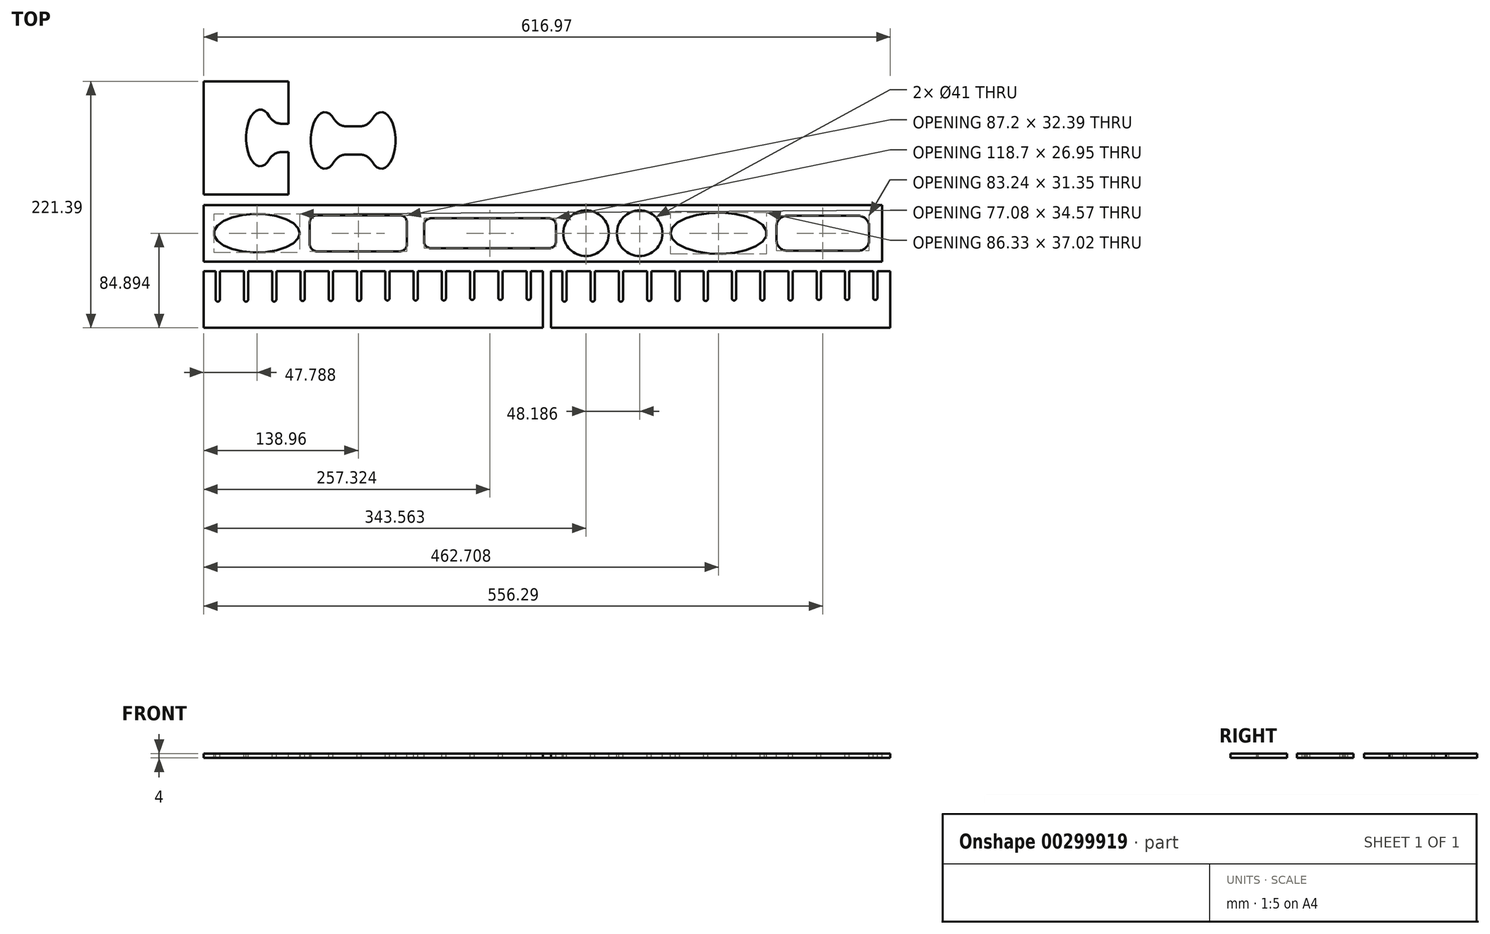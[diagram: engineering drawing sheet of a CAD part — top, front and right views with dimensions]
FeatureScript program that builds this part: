
annotation { "Feature Type Name" : "Feature", "Feature Type Description" : "" }
export const myFeature = defineFeature(function(context is Context, id is Id, definition is map)
    precondition{}
    {
        {
            var Q0;
            Q0=qCreatedBy(makeId("Top.planeOp"),FACE);
            var sketch = newSketch(context, id + "F0", { "sketchPlane" : qUnion([Q0])});
            skLineSegment(sketch, "E0.bottom", {"start": v(0, 119.79) * mm, "end": v(76.2, 119.79) * mm});
            skLineSegment(sketch, "E0.top", {"start": v(0, 221.39) * mm, "end": v(76.2, 221.39) * mm});
            skLineSegment(sketch, "E0.left", {"start": v(0, 119.79) * mm, "end": v(0, 221.39) * mm});
            skEllipticalArc(sketch, "E1", {});
            skLineSegment(sketch, "E2", {"start": v(0, 170.59) * mm, "end": v(76.2, 170.59) * mm, "construction": true});
            skLineSegment(sketch, "E3", {"start": v(70.2, 183.29) * mm, "end": v(76.2, 183.29) * mm});
            skLineSegment(sketch, "E4", {"start": v(70.2, 157.89) * mm, "end": v(76.2, 157.89) * mm});
            skLineSegment(sketch, "E5.trimOffspring", {"start": v(76.2, 183.29) * mm, "end": v(76.2, 221.39) * mm});
            skPoint(sketch, "E6.visualSharp", {"position": v(61.8, 183.29) * mm});
            skArc(sketch, "E6.filletArc", {"start": v(59.17, 189.7) * mm, "mid": v(63.82, 185) * mm, "end": v(70.2, 183.29) * mm});
            skPoint(sketch, "E7.visualSharp", {"position": v(61.8, 157.89) * mm});
            skArc(sketch, "E7.filletArc", {"start": v(70.2, 157.89) * mm, "mid": v(63.82, 156.17) * mm, "end": v(59.17, 151.48) * mm});
            skLineSegment(sketch, "E8", {"start": v(494.82, 175.08) * mm, "end": v(571.02, 175.08) * mm, "construction": true});
            skPoint(sketch, "E9.visualSharp", {"position": v(556.62, 187.78) * mm});
            skPoint(sketch, "E10.visualSharp", {"position": v(556.62, 162.38) * mm});
            skLineSegment(sketch, "E11", {"start": v(76.2, 157.89) * mm, "end": v(76.2, 119.79) * mm});
            skEllipticalArc(sketch, "E12", {});
            skLineSegment(sketch, "E13", {"start": v(128.28, 181) * mm, "end": v(134.28, 181) * mm});
            skLineSegment(sketch, "E14", {"start": v(128.28, 155.6) * mm, "end": v(134.28, 155.6) * mm});
            skPoint(sketch, "E15.visualSharp", {"position": v(119.88, 181) * mm});
            skArc(sketch, "E15.filletArc", {"start": v(117.25, 187.4) * mm, "mid": v(121.9, 182.71) * mm, "end": v(128.28, 181) * mm});
            skPoint(sketch, "E16.visualSharp", {"position": v(119.88, 155.6) * mm});
            skArc(sketch, "E16.filletArc", {"start": v(128.28, 155.6) * mm, "mid": v(121.9, 153.88) * mm, "end": v(117.25, 149.19) * mm});
            skLineSegment(sketch, "E17", {"start": v(134.28, 181) * mm, "end": v(134.28, 155.6) * mm, "construction": true});
            skLineSegment(sketch, "E18.MirrorCS", {"start": v(140.28, 155.6) * mm, "end": v(134.28, 155.6) * mm});
            skLineSegment(sketch, "E19.MirrorCS", {"start": v(140.28, 181) * mm, "end": v(134.28, 181) * mm});
            skArc(sketch, "E20.MirrorCS", {"start": v(151.3, 187.4) * mm, "mid": v(146.66, 182.71) * mm, "end": v(140.28, 181) * mm});
            skPoint(sketch, "E21.MirrorP", {"position": v(148.68, 181) * mm});
            skEllipticalArc(sketch, "E22.MirrorCS", {});
            skArc(sketch, "E23.MirrorCS", {"start": v(140.28, 155.6) * mm, "mid": v(146.66, 153.88) * mm, "end": v(151.3, 149.19) * mm});
            skPoint(sketch, "E24.MirrorP", {"position": v(148.68, 155.6) * mm});
            skLineSegment(sketch, "E25", {"start": v(190.41, 173.55) * mm, "end": v(266.61, 173.55) * mm, "construction": true});
            skPoint(sketch, "E26.visualSharp", {"position": v(252.21, 186.25) * mm});
            skPoint(sketch, "E27.visualSharp", {"position": v(252.21, 160.85) * mm});
            skLineSegment(sketch, "E28.0", {"start": v(190.44, 122.78) * mm, "end": v(190.44, 224.32) * mm});
            skLineSegment(sketch, "E28.1", {"start": v(190.44, 122.78) * mm, "end": v(266.59, 122.78) * mm});
            skLineSegment(sketch, "E28.2", {"start": v(190.44, 224.32) * mm, "end": v(266.59, 224.32) * mm});
            skLineSegment(sketch, "E28.3", {"start": v(266.59, 122.78) * mm, "end": v(266.59, 160.82) * mm});
            skLineSegment(sketch, "E28.4", {"start": v(260.61, 160.82) * mm, "end": v(266.59, 160.82) * mm});
            skArc(sketch, "E28.5", {"start": v(260.61, 160.82) * mm, "mid": v(254.25, 159.11) * mm, "end": v(249.6, 154.43) * mm});
            skLineSegment(sketch, "E28.6", {"start": v(266.59, 186.28) * mm, "end": v(266.59, 224.32) * mm});
            skLineSegment(sketch, "E28.7", {"start": v(260.61, 186.28) * mm, "end": v(266.59, 186.28) * mm});
            skArc(sketch, "E28.8", {"start": v(249.6, 192.67) * mm, "mid": v(254.25, 187.99) * mm, "end": v(260.61, 186.28) * mm});
            skFitSpline(sketch, "E28.9", {"points": [v(242.48, 198.9) * mm, v(241.21, 199.02) * mm, v(239.95, 198.9) * mm, v(238.3, 198.4) * mm, v(236.7, 197.43) * mm, v(235.2, 196.01) * mm, v(234.14, 194.73) * mm, v(233.3, 193.5) * mm, v(232.66, 192.4) * mm, v(232.2, 191.53) * mm, v(231.77, 190.61) * mm, v(231.23, 189.35) * mm, v(230.6, 187.67) * mm, v(229.97, 185.54) * mm, v(229.44, 183.3) * mm, v(229.02, 180.95) * mm, v(228.72, 178.54) * mm, v(228.56, 176.48) * mm, v(228.5, 174.81) * mm, v(228.48, 173.55) * mm, v(228.5, 172.29) * mm, v(228.56, 170.62) * mm, v(228.72, 168.56) * mm, v(229.02, 166.15) * mm, v(229.44, 163.8) * mm, v(229.97, 161.57) * mm, v(230.6, 159.43) * mm, v(231.23, 157.75) * mm, v(231.77, 156.49) * mm, v(232.2, 155.57) * mm, v(232.66, 154.7) * mm, v(233.3, 153.6) * mm, v(234.14, 152.37) * mm, v(235.2, 151.09) * mm, v(236.7, 149.67) * mm, v(238.3, 148.7) * mm, v(239.95, 148.2) * mm, v(241.21, 148.08) * mm, v(242.48, 148.2) * mm, v(244.13, 148.7) * mm, v(245.72, 149.67) * mm, v(247.22, 151.09) * mm, v(248.3, 152.37) * mm, v(249.13, 153.6) * mm, v(249.76, 154.7) * mm, v(250.22, 155.57) * mm, v(250.66, 156.49) * mm, v(251.2, 157.75) * mm, v(251.82, 159.43) * mm, v(252.46, 161.57) * mm, v(253, 163.8) * mm, v(253.4, 166.15) * mm, v(253.71, 168.56) * mm, v(253.87, 170.62) * mm, v(253.93, 172.29) * mm, v(253.94, 173.55) * mm, v(253.93, 174.81) * mm, v(253.87, 176.48) * mm, v(253.71, 178.54) * mm, v(253.4, 180.95) * mm, v(253, 183.3) * mm, v(252.46, 185.54) * mm, v(251.82, 187.67) * mm, v(251.2, 189.35) * mm, v(250.66, 190.61) * mm, v(250.22, 191.53) * mm, v(249.76, 192.4) * mm, v(249.13, 193.5) * mm, v(248.3, 194.73) * mm, v(247.22, 196.01) * mm, v(245.72, 197.43) * mm, v(244.13, 198.4) * mm, v(242.48, 198.9) * mm, v(241.21, 199.02) * mm, v(239.95, 198.9) * mm]});
            skFitSpline(sketch, "E29.9", {"points": [v(242.48, 198.9) * mm, v(241.21, 199.02) * mm, v(239.95, 198.9) * mm, v(238.3, 198.4) * mm, v(236.7, 197.43) * mm, v(235.2, 196.01) * mm, v(234.14, 194.73) * mm, v(233.3, 193.5) * mm, v(232.66, 192.4) * mm, v(232.2, 191.53) * mm, v(231.77, 190.61) * mm, v(231.23, 189.35) * mm, v(230.6, 187.67) * mm, v(229.97, 185.54) * mm, v(229.44, 183.3) * mm, v(229.02, 180.95) * mm, v(228.72, 178.54) * mm, v(228.56, 176.48) * mm, v(228.5, 174.81) * mm, v(228.48, 173.55) * mm, v(228.5, 172.29) * mm, v(228.56, 170.62) * mm, v(228.72, 168.56) * mm, v(229.02, 166.15) * mm, v(229.44, 163.8) * mm, v(229.97, 161.57) * mm, v(230.6, 159.43) * mm, v(231.23, 157.75) * mm, v(231.77, 156.49) * mm, v(232.2, 155.57) * mm, v(232.66, 154.7) * mm, v(233.3, 153.6) * mm, v(234.14, 152.37) * mm, v(235.2, 151.09) * mm, v(236.7, 149.67) * mm, v(238.3, 148.7) * mm, v(239.95, 148.2) * mm, v(241.21, 148.08) * mm, v(242.48, 148.2) * mm, v(244.13, 148.7) * mm, v(245.72, 149.67) * mm, v(247.22, 151.09) * mm, v(248.3, 152.37) * mm, v(249.13, 153.6) * mm, v(249.76, 154.7) * mm, v(250.22, 155.57) * mm, v(250.66, 156.49) * mm, v(251.2, 157.75) * mm, v(251.82, 159.43) * mm, v(252.46, 161.57) * mm, v(253, 163.8) * mm, v(253.4, 166.15) * mm, v(253.71, 168.56) * mm, v(253.87, 170.62) * mm, v(253.93, 172.29) * mm, v(253.94, 173.55) * mm, v(253.93, 174.81) * mm, v(253.87, 176.48) * mm, v(253.71, 178.54) * mm, v(253.4, 180.95) * mm, v(253, 183.3) * mm, v(252.46, 185.54) * mm, v(251.82, 187.67) * mm, v(251.2, 189.35) * mm, v(250.66, 190.61) * mm, v(250.22, 191.53) * mm, v(249.76, 192.4) * mm, v(249.13, 193.5) * mm, v(248.3, 194.73) * mm, v(247.22, 196.01) * mm, v(245.72, 197.43) * mm, v(244.13, 198.4) * mm, v(242.48, 198.9) * mm, v(241.21, 199.02) * mm, v(239.95, 198.9) * mm]});
            skLineSegment(sketch, "E30", {"start": v(291.99, 173.58) * mm, "end": v(368.19, 173.58) * mm, "construction": true});
            skPoint(sketch, "E31.visualSharp", {"position": v(353.79, 186.28) * mm});
            skPoint(sketch, "E32.visualSharp", {"position": v(353.79, 160.88) * mm});
            skLineSegment(sketch, "E33.0", {"start": v(292.04, 122.83) * mm, "end": v(292.04, 224.32) * mm});
            skLineSegment(sketch, "E33.1", {"start": v(292.04, 122.83) * mm, "end": v(368.14, 122.83) * mm});
            skLineSegment(sketch, "E33.2", {"start": v(292.04, 224.32) * mm, "end": v(368.14, 224.32) * mm});
            skLineSegment(sketch, "E33.3", {"start": v(368.14, 122.83) * mm, "end": v(368.14, 160.82) * mm});
            skLineSegment(sketch, "E33.4", {"start": v(362.19, 160.82) * mm, "end": v(368.14, 160.82) * mm});
            skArc(sketch, "E33.5", {"start": v(362.19, 160.82) * mm, "mid": v(355.84, 159.11) * mm, "end": v(351.2, 154.45) * mm});
            skLineSegment(sketch, "E33.6", {"start": v(368.14, 186.33) * mm, "end": v(368.14, 224.32) * mm});
            skLineSegment(sketch, "E33.7", {"start": v(362.19, 186.33) * mm, "end": v(368.14, 186.33) * mm});
            skArc(sketch, "E33.8", {"start": v(351.2, 192.7) * mm, "mid": v(355.84, 188.04) * mm, "end": v(362.19, 186.33) * mm});
            skFitSpline(sketch, "E33.9", {"points": [v(344.06, 198.94) * mm, v(342.79, 199.07) * mm, v(341.52, 198.94) * mm, v(339.86, 198.45) * mm, v(338.26, 197.47) * mm, v(336.76, 196.05) * mm, v(335.7, 194.77) * mm, v(334.85, 193.53) * mm, v(334.22, 192.44) * mm, v(333.76, 191.57) * mm, v(333.32, 190.65) * mm, v(332.78, 189.38) * mm, v(332.16, 187.7) * mm, v(331.52, 185.57) * mm, v(330.99, 183.32) * mm, v(330.57, 180.98) * mm, v(330.26, 178.57) * mm, v(330.11, 176.5) * mm, v(330.05, 174.84) * mm, v(330.03, 173.58) * mm, v(330.05, 172.31) * mm, v(330.11, 170.64) * mm, v(330.26, 168.58) * mm, v(330.57, 166.17) * mm, v(330.99, 163.83) * mm, v(331.52, 161.58) * mm, v(332.16, 159.45) * mm, v(332.78, 157.77) * mm, v(333.32, 156.5) * mm, v(333.76, 155.59) * mm, v(334.22, 154.71) * mm, v(334.85, 153.62) * mm, v(335.7, 152.38) * mm, v(336.76, 151.1) * mm, v(338.26, 149.68) * mm, v(339.86, 148.7) * mm, v(341.52, 148.2) * mm, v(342.79, 148.08) * mm, v(344.06, 148.2) * mm, v(345.72, 148.7) * mm, v(347.31, 149.68) * mm, v(348.82, 151.1) * mm, v(349.89, 152.38) * mm, v(350.73, 153.62) * mm, v(351.36, 154.71) * mm, v(351.82, 155.59) * mm, v(352.25, 156.5) * mm, v(352.8, 157.77) * mm, v(353.42, 159.45) * mm, v(354.06, 161.58) * mm, v(354.6, 163.83) * mm, v(355, 166.17) * mm, v(355.31, 168.58) * mm, v(355.47, 170.64) * mm, v(355.53, 172.31) * mm, v(355.54, 173.58) * mm, v(355.53, 174.84) * mm, v(355.47, 176.5) * mm, v(355.31, 178.57) * mm, v(355, 180.98) * mm, v(354.6, 183.32) * mm, v(354.06, 185.57) * mm, v(353.42, 187.7) * mm, v(352.8, 189.38) * mm, v(352.25, 190.65) * mm, v(351.82, 191.57) * mm, v(351.36, 192.44) * mm, v(350.73, 193.53) * mm, v(349.89, 194.77) * mm, v(348.82, 196.05) * mm, v(347.31, 197.47) * mm, v(345.72, 198.45) * mm, v(344.06, 198.94) * mm, v(342.79, 199.07) * mm, v(341.52, 198.94) * mm]});
            skLineSegment(sketch, "E34", {"start": v(400.26, 175.1) * mm, "end": v(476.46, 175.1) * mm, "construction": true});
            skPoint(sketch, "E35.visualSharp", {"position": v(462.06, 187.8) * mm});
            skPoint(sketch, "E36.visualSharp", {"position": v(462.06, 162.4) * mm});
            skLineSegment(sketch, "E37.0", {"start": v(400.33, 124.38) * mm, "end": v(400.33, 225.82) * mm});
            skLineSegment(sketch, "E37.1", {"start": v(400.33, 124.38) * mm, "end": v(476.38, 124.38) * mm});
            skLineSegment(sketch, "E37.2", {"start": v(400.33, 225.82) * mm, "end": v(476.38, 225.82) * mm});
            skLineSegment(sketch, "E37.3", {"start": v(476.38, 124.38) * mm, "end": v(476.38, 162.32) * mm});
            skLineSegment(sketch, "E37.4", {"start": v(470.46, 162.32) * mm, "end": v(476.38, 162.32) * mm});
            skArc(sketch, "E37.5", {"start": v(470.46, 162.32) * mm, "mid": v(464.12, 160.62) * mm, "end": v(459.5, 155.96) * mm});
            skLineSegment(sketch, "E37.6", {"start": v(476.38, 187.88) * mm, "end": v(476.38, 225.82) * mm});
            skLineSegment(sketch, "E37.7", {"start": v(470.46, 187.88) * mm, "end": v(476.38, 187.88) * mm});
            skArc(sketch, "E37.8", {"start": v(459.5, 194.24) * mm, "mid": v(464.12, 189.58) * mm, "end": v(470.46, 187.88) * mm});
            skFitSpline(sketch, "E37.9", {"points": [v(452.33, 200.5) * mm, v(451.06, 200.62) * mm, v(449.78, 200.5) * mm, v(448.12, 200) * mm, v(446.52, 199.02) * mm, v(445.01, 197.6) * mm, v(443.94, 196.31) * mm, v(443.1, 195.07) * mm, v(442.46, 193.98) * mm, v(442, 193.1) * mm, v(441.57, 192.19) * mm, v(441.02, 190.92) * mm, v(440.4, 189.24) * mm, v(439.76, 187.1) * mm, v(439.23, 184.85) * mm, v(438.81, 182.51) * mm, v(438.5, 180.1) * mm, v(438.35, 178.03) * mm, v(438.3, 176.36) * mm, v(438.28, 175.1) * mm, v(438.3, 173.84) * mm, v(438.35, 172.17) * mm, v(438.5, 170.1) * mm, v(438.81, 167.69) * mm, v(439.23, 165.35) * mm, v(439.76, 163.1) * mm, v(440.4, 160.96) * mm, v(441.02, 159.29) * mm, v(441.57, 158.02) * mm, v(442, 157.1) * mm, v(442.46, 156.23) * mm, v(443.1, 155.13) * mm, v(443.94, 153.89) * mm, v(445.01, 152.6) * mm, v(446.52, 151.18) * mm, v(448.12, 150.2) * mm, v(449.78, 149.7) * mm, v(451.06, 149.58) * mm, v(452.33, 149.7) * mm, v(454, 150.2) * mm, v(455.6, 151.18) * mm, v(457.1, 152.6) * mm, v(458.18, 153.89) * mm, v(459.02, 155.13) * mm, v(459.65, 156.23) * mm, v(460.1, 157.1) * mm, v(460.55, 158.02) * mm, v(461.1, 159.29) * mm, v(461.71, 160.96) * mm, v(462.35, 163.1) * mm, v(462.88, 165.35) * mm, v(463.3, 167.69) * mm, v(463.6, 170.1) * mm, v(463.76, 172.17) * mm, v(463.82, 173.84) * mm, v(463.84, 175.1) * mm, v(463.82, 176.36) * mm, v(463.76, 178.03) * mm, v(463.6, 180.1) * mm, v(463.3, 182.51) * mm, v(462.88, 184.85) * mm, v(462.35, 187.1) * mm, v(461.71, 189.24) * mm, v(461.1, 190.92) * mm, v(460.55, 192.19) * mm, v(460.1, 193.1) * mm, v(459.65, 193.98) * mm, v(459.02, 195.07) * mm, v(458.18, 196.31) * mm, v(457.1, 197.6) * mm, v(455.6, 199.02) * mm, v(454, 200) * mm, v(452.33, 200.5) * mm, v(451.06, 200.62) * mm, v(449.78, 200.5) * mm]});
            skLineSegment(sketch, "E38.0", {"start": v(494.92, 124.38) * mm, "end": v(494.92, 225.77) * mm});
            skLineSegment(sketch, "E38.1", {"start": v(494.92, 124.38) * mm, "end": v(570.92, 124.38) * mm});
            skLineSegment(sketch, "E38.2", {"start": v(494.92, 225.77) * mm, "end": v(570.92, 225.77) * mm});
            skLineSegment(sketch, "E38.3", {"start": v(570.92, 124.38) * mm, "end": v(570.92, 162.27) * mm});
            skLineSegment(sketch, "E38.4", {"start": v(565.02, 162.27) * mm, "end": v(570.92, 162.27) * mm});
            skArc(sketch, "E38.5", {"start": v(565.02, 162.27) * mm, "mid": v(558.7, 160.57) * mm, "end": v(554.08, 155.92) * mm});
            skLineSegment(sketch, "E38.6", {"start": v(570.92, 187.88) * mm, "end": v(570.92, 225.77) * mm});
            skLineSegment(sketch, "E38.7", {"start": v(565.02, 187.88) * mm, "end": v(570.92, 187.88) * mm});
            skArc(sketch, "E38.8", {"start": v(554.08, 194.23) * mm, "mid": v(558.7, 189.58) * mm, "end": v(565.02, 187.88) * mm});
            skFitSpline(sketch, "E38.9", {"points": [v(546.9, 200.5) * mm, v(545.62, 200.62) * mm, v(544.34, 200.5) * mm, v(542.67, 200) * mm, v(541.07, 199.01) * mm, v(539.56, 197.59) * mm, v(538.48, 196.3) * mm, v(537.64, 195.06) * mm, v(537, 193.96) * mm, v(536.55, 193.09) * mm, v(536.11, 192.17) * mm, v(535.56, 190.9) * mm, v(534.94, 189.22) * mm, v(534.3, 187.08) * mm, v(533.77, 184.83) * mm, v(533.35, 182.5) * mm, v(533.05, 180.07) * mm, v(532.9, 178.01) * mm, v(532.83, 176.34) * mm, v(532.82, 175.08) * mm, v(532.83, 173.81) * mm, v(532.9, 172.14) * mm, v(533.05, 170.08) * mm, v(533.35, 167.66) * mm, v(533.77, 165.32) * mm, v(534.3, 163.07) * mm, v(534.94, 160.93) * mm, v(535.56, 159.25) * mm, v(536.11, 157.98) * mm, v(536.55, 157.06) * mm, v(537, 156.19) * mm, v(537.64, 155.1) * mm, v(538.48, 153.85) * mm, v(539.56, 152.56) * mm, v(541.07, 151.14) * mm, v(542.67, 150.16) * mm, v(544.34, 149.66) * mm, v(545.62, 149.53) * mm, v(546.9, 149.66) * mm, v(548.57, 150.16) * mm, v(550.18, 151.14) * mm, v(551.69, 152.56) * mm, v(552.76, 153.85) * mm, v(553.6, 155.1) * mm, v(554.24, 156.19) * mm, v(554.7, 157.06) * mm, v(555.13, 157.98) * mm, v(555.68, 159.25) * mm, v(556.3, 160.93) * mm, v(556.94, 163.07) * mm, v(557.47, 165.32) * mm, v(557.9, 167.66) * mm, v(558.2, 170.08) * mm, v(558.35, 172.14) * mm, v(558.41, 173.81) * mm, v(558.43, 175.08) * mm, v(558.41, 176.34) * mm, v(558.35, 178.01) * mm, v(558.2, 180.07) * mm, v(557.9, 182.5) * mm, v(557.47, 184.83) * mm, v(556.94, 187.08) * mm, v(556.3, 189.22) * mm, v(555.68, 190.9) * mm, v(555.13, 192.17) * mm, v(554.7, 193.09) * mm, v(554.24, 193.96) * mm, v(553.6, 195.06) * mm, v(552.76, 196.3) * mm, v(551.69, 197.59) * mm, v(550.18, 199.01) * mm, v(548.57, 200) * mm, v(546.9, 200.5) * mm, v(545.62, 200.62) * mm, v(544.34, 200.5) * mm]});
            skLineSegment(sketch, "E39.bottom", {"start": v(0, 0) * mm, "end": v(304.8, 0) * mm});
            skLineSegment(sketch, "E39.top", {"start": v(0, 50.8) * mm, "end": v(10.75, 50.8) * mm});
            skLineSegment(sketch, "E39.left", {"start": v(0, 0) * mm, "end": v(0, 50.8) * mm});
            skLineSegment(sketch, "E39.right", {"start": v(304.8, 0) * mm, "end": v(304.8, 50.8) * mm});
            skLineSegment(sketch, "E40.direction1", {"start": v(12.64, 25.4) * mm, "end": v(38.04, 25.4) * mm, "construction": true});
            skArc(sketch, "E41.0.endCap", {"start": v(14.54, 25.4) * mm, "mid": v(12.64, 23.5) * mm, "end": v(10.75, 25.4) * mm});
            skLineSegment(sketch, "E41.0.left", {"start": v(14.54, 50.8) * mm, "end": v(14.54, 25.4) * mm});
            skLineSegment(sketch, "E41.0.right", {"start": v(10.75, 50.8) * mm, "end": v(10.75, 25.4) * mm});
            skArc(sketch, "E42.0.endCap", {"start": v(39.94, 25.4) * mm, "mid": v(38.04, 23.5) * mm, "end": v(36.14, 25.4) * mm});
            skLineSegment(sketch, "E42.0.left", {"start": v(39.94, 50.8) * mm, "end": v(39.94, 25.4) * mm});
            skLineSegment(sketch, "E42.0.right", {"start": v(36.14, 50.8) * mm, "end": v(36.14, 25.4) * mm});
            skArc(sketch, "E43.0.endCap", {"start": v(65.26, 25.4) * mm, "mid": v(63.35, 23.5) * mm, "end": v(61.45, 25.4) * mm});
            skLineSegment(sketch, "E43.0.left", {"start": v(65.26, 50.8) * mm, "end": v(65.26, 25.4) * mm});
            skLineSegment(sketch, "E43.0.right", {"start": v(61.45, 50.8) * mm, "end": v(61.45, 25.4) * mm});
            skLineSegment(sketch, "E44.direction1", {"start": v(88.85, 25.9) * mm, "end": v(114.25, 25.9) * mm, "construction": true});
            skArc(sketch, "E45.0.endCap", {"start": v(90.74, 25.9) * mm, "mid": v(88.85, 24) * mm, "end": v(86.95, 25.9) * mm});
            skLineSegment(sketch, "E45.0.left", {"start": v(90.74, 50.8) * mm, "end": v(90.74, 25.9) * mm});
            skLineSegment(sketch, "E45.0.right", {"start": v(86.95, 50.8) * mm, "end": v(86.95, 25.9) * mm});
            skArc(sketch, "E46.0.endCap", {"start": v(116.15, 25.9) * mm, "mid": v(114.25, 24) * mm, "end": v(112.35, 25.9) * mm});
            skLineSegment(sketch, "E46.0.left", {"start": v(116.15, 50.8) * mm, "end": v(116.15, 25.9) * mm});
            skLineSegment(sketch, "E46.0.right", {"start": v(112.35, 50.8) * mm, "end": v(112.35, 25.9) * mm});
            skArc(sketch, "E47.0.endCap", {"start": v(141.46, 25.9) * mm, "mid": v(139.56, 24) * mm, "end": v(137.65, 25.9) * mm});
            skLineSegment(sketch, "E47.0.left", {"start": v(141.46, 50.8) * mm, "end": v(141.46, 25.9) * mm});
            skLineSegment(sketch, "E47.0.right", {"start": v(137.65, 50.8) * mm, "end": v(137.65, 25.9) * mm});
            skLineSegment(sketch, "E48.direction1", {"start": v(165.05, 26.4) * mm, "end": v(190.45, 26.4) * mm, "construction": true});
            skArc(sketch, "E49.0.endCap", {"start": v(166.94, 26.4) * mm, "mid": v(165.05, 24.5) * mm, "end": v(163.15, 26.4) * mm});
            skLineSegment(sketch, "E49.0.left", {"start": v(166.94, 50.8) * mm, "end": v(166.94, 26.4) * mm});
            skLineSegment(sketch, "E49.0.right", {"start": v(163.15, 50.8) * mm, "end": v(163.15, 26.4) * mm});
            skArc(sketch, "E50.0.endCap", {"start": v(192.35, 26.4) * mm, "mid": v(190.45, 24.5) * mm, "end": v(188.55, 26.4) * mm});
            skLineSegment(sketch, "E50.0.left", {"start": v(192.35, 50.8) * mm, "end": v(192.35, 26.4) * mm});
            skLineSegment(sketch, "E50.0.right", {"start": v(188.55, 50.8) * mm, "end": v(188.55, 26.4) * mm});
            skArc(sketch, "E51.0.endCap", {"start": v(217.66, 26.4) * mm, "mid": v(215.75, 24.5) * mm, "end": v(213.85, 26.4) * mm});
            skLineSegment(sketch, "E51.0.left", {"start": v(217.66, 50.8) * mm, "end": v(217.66, 26.4) * mm});
            skLineSegment(sketch, "E51.0.right", {"start": v(213.85, 50.8) * mm, "end": v(213.85, 26.4) * mm});
            skLineSegment(sketch, "E52.direction1", {"start": v(241.25, 26.9) * mm, "end": v(266.64, 26.9) * mm, "construction": true});
            skArc(sketch, "E53.0.endCap", {"start": v(243.14, 26.9) * mm, "mid": v(241.25, 25) * mm, "end": v(239.35, 26.9) * mm});
            skLineSegment(sketch, "E53.0.left", {"start": v(243.14, 50.8) * mm, "end": v(243.14, 26.9) * mm});
            skLineSegment(sketch, "E53.0.right", {"start": v(239.35, 50.8) * mm, "end": v(239.35, 26.9) * mm});
            skArc(sketch, "E54.0.endCap", {"start": v(268.54, 26.9) * mm, "mid": v(266.64, 25) * mm, "end": v(264.75, 26.9) * mm});
            skLineSegment(sketch, "E54.0.left", {"start": v(268.54, 50.8) * mm, "end": v(268.54, 26.9) * mm});
            skLineSegment(sketch, "E54.0.right", {"start": v(264.74, 50.8) * mm, "end": v(264.74, 26.9) * mm});
            skArc(sketch, "E55.0.endCap", {"start": v(293.86, 26.9) * mm, "mid": v(291.96, 25) * mm, "end": v(290.05, 26.9) * mm});
            skLineSegment(sketch, "E55.0.left", {"start": v(293.86, 50.8) * mm, "end": v(293.86, 26.9) * mm});
            skLineSegment(sketch, "E55.0.right", {"start": v(290.05, 50.8) * mm, "end": v(290.05, 26.9) * mm});
            skLineSegment(sketch, "E56.trimOffspring", {"start": v(14.54, 50.8) * mm, "end": v(36.14, 50.8) * mm});
            skLineSegment(sketch, "E57.trimOffspring", {"start": v(39.94, 50.8) * mm, "end": v(61.45, 50.8) * mm});
            skLineSegment(sketch, "E58.trimOffspring", {"start": v(65.26, 50.8) * mm, "end": v(86.95, 50.8) * mm});
            skLineSegment(sketch, "E59.trimOffspring", {"start": v(90.74, 50.8) * mm, "end": v(112.35, 50.8) * mm});
            skLineSegment(sketch, "E60.trimOffspring", {"start": v(116.15, 50.8) * mm, "end": v(137.65, 50.8) * mm});
            skLineSegment(sketch, "E61.trimOffspring", {"start": v(141.46, 50.8) * mm, "end": v(163.15, 50.8) * mm});
            skLineSegment(sketch, "E62.trimOffspring", {"start": v(166.94, 50.8) * mm, "end": v(188.55, 50.8) * mm});
            skLineSegment(sketch, "E63.trimOffspring", {"start": v(192.35, 50.8) * mm, "end": v(213.85, 50.8) * mm});
            skLineSegment(sketch, "E64.trimOffspring", {"start": v(217.66, 50.8) * mm, "end": v(239.35, 50.8) * mm});
            skLineSegment(sketch, "E65.trimOffspring", {"start": v(243.14, 50.8) * mm, "end": v(264.74, 50.8) * mm});
            skLineSegment(sketch, "E66.trimOffspring", {"start": v(268.54, 50.8) * mm, "end": v(290.05, 50.8) * mm});
            skLineSegment(sketch, "E67.trimOffspring", {"start": v(293.86, 50.8) * mm, "end": v(304.8, 50.8) * mm});
            skLineSegment(sketch, "E68.bottom", {"start": v(0, 59.5) * mm, "end": v(609.6, 59.5) * mm});
            skLineSegment(sketch, "E68.top", {"start": v(0, 110.3) * mm, "end": v(609.6, 110.3) * mm});
            skLineSegment(sketch, "E68.left", {"start": v(0, 59.5) * mm, "end": v(0, 110.3) * mm});
            skLineSegment(sketch, "E68.right", {"start": v(609.6, 59.5) * mm, "end": v(609.6, 110.3) * mm});
            skEllipse(sketch, "E69", {"center": v(47.79, 84.9) * mm, "majorRadius": 38.54 * mm, "minorRadius": 17.29 * mm, "majorAxis": v(1, 0)});
            skPoint(sketch, "E69.centerSnap0", {"position": v(0, 84.9) * mm});
            skLineSegment(sketch, "E70.bottom", {"start": v(101.7, 101.09) * mm, "end": v(176.21, 101.09) * mm});
            skLineSegment(sketch, "E70.top", {"start": v(101.7, 68.7) * mm, "end": v(176.21, 68.7) * mm});
            skLineSegment(sketch, "E70.left", {"start": v(95.36, 94.74) * mm, "end": v(95.36, 75.05) * mm});
            skLineSegment(sketch, "E70.right", {"start": v(182.56, 94.74) * mm, "end": v(182.56, 75.05) * mm});
            skPoint(sketch, "E70.middle", {"position": v(138.96, 84.9) * mm});
            skPoint(sketch, "E70.middle.positionSnap0", {"position": v(86.33, 84.9) * mm});
            skPoint(sketch, "E70.centerSnap0", {"position": v(86.33, 84.9) * mm});
            skPoint(sketch, "E71.visualSharp", {"position": v(95.36, 101.09) * mm});
            skArc(sketch, "E71.filletArc", {"start": v(101.7, 101.09) * mm, "mid": v(97.22, 99.23) * mm, "end": v(95.36, 94.74) * mm});
            skPoint(sketch, "E72.visualSharp", {"position": v(182.56, 101.09) * mm});
            skArc(sketch, "E72.filletArc", {"start": v(182.56, 94.74) * mm, "mid": v(180.7, 99.23) * mm, "end": v(176.21, 101.09) * mm});
            skPoint(sketch, "E73.visualSharp", {"position": v(182.56, 68.7) * mm});
            skArc(sketch, "E73.filletArc", {"start": v(176.21, 68.7) * mm, "mid": v(180.7, 70.56) * mm, "end": v(182.56, 75.05) * mm});
            skPoint(sketch, "E74.visualSharp", {"position": v(95.36, 68.7) * mm});
            skArc(sketch, "E74.filletArc", {"start": v(95.36, 75.05) * mm, "mid": v(97.22, 70.56) * mm, "end": v(101.7, 68.7) * mm});
            skLineSegment(sketch, "E75.bottom", {"start": v(204.32, 98.37) * mm, "end": v(310.32, 98.37) * mm});
            skLineSegment(sketch, "E75.top", {"start": v(204.32, 71.42) * mm, "end": v(310.32, 71.42) * mm});
            skLineSegment(sketch, "E75.left", {"start": v(197.97, 92.02) * mm, "end": v(197.97, 77.77) * mm});
            skLineSegment(sketch, "E75.right", {"start": v(316.67, 92.02) * mm, "end": v(316.67, 77.77) * mm});
            skPoint(sketch, "E75.middle", {"position": v(257.32, 84.9) * mm});
            skPoint(sketch, "E75.middle.positionSnap0", {"position": v(182.56, 84.9) * mm});
            skPoint(sketch, "E75.centerSnap0", {"position": v(182.56, 84.9) * mm});
            skPoint(sketch, "E76.visualSharp", {"position": v(197.97, 98.37) * mm});
            skArc(sketch, "E76.filletArc", {"start": v(204.32, 98.37) * mm, "mid": v(199.83, 96.51) * mm, "end": v(197.97, 92.02) * mm});
            skPoint(sketch, "E77.visualSharp", {"position": v(197.97, 71.42) * mm});
            skArc(sketch, "E77.filletArc", {"start": v(197.97, 77.77) * mm, "mid": v(199.83, 73.28) * mm, "end": v(204.32, 71.42) * mm});
            skPoint(sketch, "E78.visualSharp", {"position": v(316.67, 71.42) * mm});
            skArc(sketch, "E78.filletArc", {"start": v(310.32, 71.42) * mm, "mid": v(314.81, 73.28) * mm, "end": v(316.67, 77.77) * mm});
            skPoint(sketch, "E79.visualSharp", {"position": v(316.67, 98.37) * mm});
            skArc(sketch, "E79.filletArc", {"start": v(316.67, 92.02) * mm, "mid": v(314.81, 96.51) * mm, "end": v(310.32, 98.37) * mm});
            skCircle(sketch, "E80", {"center": v(343.56, 84.9) * mm, "radius": 20.5 * mm});
            skCircle(sketch, "E81", {"center": v(391.75, 84.9) * mm, "radius": 20.5 * mm});
            skEllipse(sketch, "E82", {"center": v(462.7, 84.9) * mm, "majorRadius": 43.16 * mm, "minorRadius": 18.51 * mm, "majorAxis": v(-1, 0)});
            skPoint(sketch, "E82.centerSnap0", {"position": v(609.6, 84.9) * mm});
            skLineSegment(sketch, "E83.bottom", {"start": v(524.2, 100.57) * mm, "end": v(588.39, 100.57) * mm});
            skLineSegment(sketch, "E83.top", {"start": v(524.2, 69.22) * mm, "end": v(588.39, 69.22) * mm});
            skLineSegment(sketch, "E83.left", {"start": v(514.67, 91.04) * mm, "end": v(514.67, 78.75) * mm});
            skLineSegment(sketch, "E83.right", {"start": v(597.91, 91.04) * mm, "end": v(597.91, 78.75) * mm});
            skPoint(sketch, "E83.middle", {"position": v(556.3, 84.9) * mm});
            skPoint(sketch, "E84.visualSharp", {"position": v(514.67, 100.57) * mm});
            skArc(sketch, "E84.filletArc", {"start": v(524.2, 100.57) * mm, "mid": v(517.46, 97.78) * mm, "end": v(514.67, 91.04) * mm});
            skPoint(sketch, "E85.visualSharp", {"position": v(597.91, 100.57) * mm});
            skArc(sketch, "E85.filletArc", {"start": v(597.91, 91.04) * mm, "mid": v(595.12, 97.78) * mm, "end": v(588.39, 100.57) * mm});
            skPoint(sketch, "E86.visualSharp", {"position": v(597.91, 69.22) * mm});
            skArc(sketch, "E86.filletArc", {"start": v(588.39, 69.22) * mm, "mid": v(595.12, 72.01) * mm, "end": v(597.91, 78.75) * mm});
            skPoint(sketch, "E87.visualSharp", {"position": v(514.67, 69.22) * mm});
            skArc(sketch, "E87.filletArc", {"start": v(514.67, 78.75) * mm, "mid": v(517.46, 72.01) * mm, "end": v(524.2, 69.22) * mm});
            skLineSegment(sketch, "E88.bottom", {"start": v(312.17, 0) * mm, "end": v(616.97, 0) * mm});
            skLineSegment(sketch, "E88.top", {"start": v(312.17, 50.8) * mm, "end": v(322.27, 50.8) * mm});
            skLineSegment(sketch, "E88.left", {"start": v(312.17, 0) * mm, "end": v(312.17, 50.8) * mm});
            skLineSegment(sketch, "E88.right", {"start": v(616.97, 0) * mm, "end": v(616.97, 50.8) * mm});
            skLineSegment(sketch, "E89.direction1", {"start": v(324.16, 25.4) * mm, "end": v(349.56, 25.4) * mm, "construction": true});
            skArc(sketch, "E90.0.endCap", {"start": v(326.06, 25.4) * mm, "mid": v(324.16, 23.5) * mm, "end": v(322.27, 25.4) * mm});
            skLineSegment(sketch, "E90.0.left", {"start": v(326.06, 50.8) * mm, "end": v(326.06, 25.4) * mm});
            skLineSegment(sketch, "E90.0.right", {"start": v(322.27, 50.8) * mm, "end": v(322.27, 25.4) * mm});
            skArc(sketch, "E91.0.endCap", {"start": v(351.46, 25.4) * mm, "mid": v(349.56, 23.5) * mm, "end": v(347.66, 25.4) * mm});
            skLineSegment(sketch, "E91.0.left", {"start": v(351.46, 50.8) * mm, "end": v(351.46, 25.4) * mm});
            skLineSegment(sketch, "E91.0.right", {"start": v(347.66, 50.8) * mm, "end": v(347.66, 25.4) * mm});
            skArc(sketch, "E92.0.endCap", {"start": v(376.78, 25.4) * mm, "mid": v(374.87, 23.5) * mm, "end": v(372.97, 25.4) * mm});
            skLineSegment(sketch, "E92.0.left", {"start": v(376.78, 50.8) * mm, "end": v(376.78, 25.4) * mm});
            skLineSegment(sketch, "E92.0.right", {"start": v(372.97, 50.8) * mm, "end": v(372.97, 25.4) * mm});
            skLineSegment(sketch, "E93.direction1", {"start": v(400.36, 25.9) * mm, "end": v(425.76, 25.9) * mm, "construction": true});
            skArc(sketch, "E94.0.endCap", {"start": v(402.26, 25.9) * mm, "mid": v(400.36, 24) * mm, "end": v(398.47, 25.9) * mm});
            skLineSegment(sketch, "E94.0.left", {"start": v(402.26, 50.8) * mm, "end": v(402.26, 25.9) * mm});
            skLineSegment(sketch, "E94.0.right", {"start": v(398.47, 50.8) * mm, "end": v(398.47, 25.9) * mm});
            skArc(sketch, "E95.0.endCap", {"start": v(427.66, 25.9) * mm, "mid": v(425.76, 24) * mm, "end": v(423.86, 25.9) * mm});
            skLineSegment(sketch, "E95.0.left", {"start": v(427.66, 50.8) * mm, "end": v(427.66, 25.9) * mm});
            skLineSegment(sketch, "E95.0.right", {"start": v(423.86, 50.8) * mm, "end": v(423.86, 25.9) * mm});
            skArc(sketch, "E96.0.endCap", {"start": v(452.98, 25.9) * mm, "mid": v(451.07, 24) * mm, "end": v(449.17, 25.9) * mm});
            skLineSegment(sketch, "E96.0.left", {"start": v(452.98, 50.8) * mm, "end": v(452.98, 25.9) * mm});
            skLineSegment(sketch, "E96.0.right", {"start": v(449.17, 50.8) * mm, "end": v(449.17, 25.9) * mm});
            skLineSegment(sketch, "E97.direction1", {"start": v(476.56, 26.4) * mm, "end": v(501.96, 26.4) * mm, "construction": true});
            skArc(sketch, "E98.0.endCap", {"start": v(478.46, 26.4) * mm, "mid": v(476.56, 24.5) * mm, "end": v(474.67, 26.4) * mm});
            skLineSegment(sketch, "E98.0.left", {"start": v(478.46, 50.8) * mm, "end": v(478.46, 26.4) * mm});
            skLineSegment(sketch, "E98.0.right", {"start": v(474.67, 50.8) * mm, "end": v(474.67, 26.4) * mm});
            skArc(sketch, "E99.0.endCap", {"start": v(503.86, 26.4) * mm, "mid": v(501.96, 24.5) * mm, "end": v(500.06, 26.4) * mm});
            skLineSegment(sketch, "E99.0.left", {"start": v(503.86, 50.8) * mm, "end": v(503.86, 26.4) * mm});
            skLineSegment(sketch, "E99.0.right", {"start": v(500.06, 50.8) * mm, "end": v(500.06, 26.4) * mm});
            skArc(sketch, "E100.0.endCap", {"start": v(529.18, 26.4) * mm, "mid": v(527.27, 24.5) * mm, "end": v(525.37, 26.4) * mm});
            skLineSegment(sketch, "E100.0.left", {"start": v(529.18, 50.8) * mm, "end": v(529.18, 26.4) * mm});
            skLineSegment(sketch, "E100.0.right", {"start": v(525.37, 50.8) * mm, "end": v(525.37, 26.4) * mm});
            skLineSegment(sketch, "E101.direction1", {"start": v(552.76, 26.9) * mm, "end": v(578.16, 26.9) * mm, "construction": true});
            skArc(sketch, "E102.0.endCap", {"start": v(554.66, 26.9) * mm, "mid": v(552.76, 25) * mm, "end": v(550.87, 26.9) * mm});
            skLineSegment(sketch, "E102.0.left", {"start": v(554.66, 50.8) * mm, "end": v(554.66, 26.9) * mm});
            skLineSegment(sketch, "E102.0.right", {"start": v(550.87, 50.8) * mm, "end": v(550.87, 26.9) * mm});
            skArc(sketch, "E103.0.endCap", {"start": v(580.06, 26.9) * mm, "mid": v(578.16, 25) * mm, "end": v(576.26, 26.9) * mm});
            skLineSegment(sketch, "E103.0.left", {"start": v(580.06, 50.8) * mm, "end": v(580.06, 26.9) * mm});
            skLineSegment(sketch, "E103.0.right", {"start": v(576.26, 50.8) * mm, "end": v(576.26, 26.9) * mm});
            skArc(sketch, "E104.0.endCap", {"start": v(605.38, 26.9) * mm, "mid": v(603.47, 25) * mm, "end": v(601.57, 26.9) * mm});
            skLineSegment(sketch, "E104.0.left", {"start": v(605.38, 50.8) * mm, "end": v(605.38, 26.9) * mm});
            skLineSegment(sketch, "E104.0.right", {"start": v(601.57, 50.8) * mm, "end": v(601.57, 26.9) * mm});
            skLineSegment(sketch, "E105.trimOffspring", {"start": v(326.06, 50.8) * mm, "end": v(347.66, 50.8) * mm});
            skLineSegment(sketch, "E106.trimOffspring", {"start": v(351.46, 50.8) * mm, "end": v(372.97, 50.8) * mm});
            skLineSegment(sketch, "E107.trimOffspring", {"start": v(376.78, 50.8) * mm, "end": v(398.47, 50.8) * mm});
            skLineSegment(sketch, "E108.trimOffspring", {"start": v(402.26, 50.8) * mm, "end": v(423.86, 50.8) * mm});
            skLineSegment(sketch, "E109.trimOffspring", {"start": v(427.66, 50.8) * mm, "end": v(449.17, 50.8) * mm});
            skLineSegment(sketch, "E110.trimOffspring", {"start": v(452.98, 50.8) * mm, "end": v(474.67, 50.8) * mm});
            skLineSegment(sketch, "E111.trimOffspring", {"start": v(478.46, 50.8) * mm, "end": v(500.06, 50.8) * mm});
            skLineSegment(sketch, "E112.trimOffspring", {"start": v(503.86, 50.8) * mm, "end": v(525.37, 50.8) * mm});
            skLineSegment(sketch, "E113.trimOffspring", {"start": v(529.18, 50.8) * mm, "end": v(550.87, 50.8) * mm});
            skLineSegment(sketch, "E114.trimOffspring", {"start": v(554.66, 50.8) * mm, "end": v(576.26, 50.8) * mm});
            skLineSegment(sketch, "E115.trimOffspring", {"start": v(580.06, 50.8) * mm, "end": v(601.57, 50.8) * mm});
            skLineSegment(sketch, "E116.trimOffspring", {"start": v(605.38, 50.8) * mm, "end": v(616.97, 50.8) * mm});
            const initialGuessF0  = {"E1": [0.0508, 0.17058822201490403, 0, 1, 0.0254, 0.0127, 5.563731595720363, 3.8610463650490146], "E12": [0.10887801727700261, 0.16829481958790887, 0, 1, 0.0254, 0.0127, 5.563731595720363, 3.861046365049013], "E22.MirrorCS": [0.15967801727700262, 0.16829481958790887, 0, 1, 0.0254, 0.0127, 2.422138942130573, 0.7194537114592233]};
            skSetInitialGuess(sketch, initialGuessF0);
            skSolve(sketch);
        }
        {
            var Q0;
            Q0=makeQuery(id+"F0.imprint","IMPRINT",FACE,{"disambiguationData":[TD([[makeQuery(id+"F0.imprint","IMPRINT",EDGE,{"derivedFrom":sQuery(id+"F0.wireOp",EDGE,"3ff6de3b-4239-4394-abdc-ca870c27d29f.bottom")}),1.0]])]});
            var Q1;
            Q1=makeQuery(id+"F0.imprint","IMPRINT",FACE,{"disambiguationData":[TD([[makeQuery(id+"F0.imprint","IMPRINT",EDGE,{"derivedFrom":sQuery(id+"F0.wireOp",EDGE,"E12")}),1.0]])]});
            var Q2;
            Q2=makeQuery(id+"F0.imprint","IMPRINT",FACE,{"disambiguationData":[TD([[makeQuery(id+"F0.imprint","IMPRINT",EDGE,{"derivedFrom":sQuery(id+"F0.wireOp",EDGE,"E28.0")}),-1.0]])]});
            var Q3;
            Q3=makeQuery(id+"F0.imprint","IMPRINT",FACE,{"disambiguationData":[TD([[makeQuery(id+"F0.imprint","IMPRINT",EDGE,{"derivedFrom":sQuery(id+"F0.wireOp",EDGE,"E33.0")}),-1.0]])]});
            var Q4;
            Q4=makeQuery(id+"F0.imprint","IMPRINT",FACE,{"disambiguationData":[TD([[makeQuery(id+"F0.imprint","IMPRINT",EDGE,{"derivedFrom":sQuery(id+"F0.wireOp",EDGE,"E37.0")}),-1.0]])]});
            var Q5;
            Q5=makeQuery(id+"F0.imprint","IMPRINT",FACE,{"disambiguationData":[TD([[makeQuery(id+"F0.imprint","IMPRINT",EDGE,{"derivedFrom":sQuery(id+"F0.wireOp",EDGE,"E38.0")}),-1.0]])]});
            var Q6;
            Q6=makeQuery(id+"F0.imprint","IMPRINT",FACE,{"disambiguationData":[TD([[makeQuery(id+"F0.imprint","IMPRINT",EDGE,{"derivedFrom":sQuery(id+"F0.wireOp",EDGE,"E0.bottom")}),1.0]])]});
            var Q7;
            Q7=makeQuery(id+"F0.imprint","IMPRINT",FACE,{"disambiguationData":[TD([[makeQuery(id+"F0.imprint","IMPRINT",EDGE,{"derivedFrom":sQuery(id+"F0.wireOp",EDGE,"E39.bottom")}),1.0]])]});
            var Q8;
            Q8=makeQuery(id+"F0.imprint","IMPRINT",FACE,{"disambiguationData":[TD([[makeQuery(id+"F0.imprint","IMPRINT",EDGE,{"derivedFrom":sQuery(id+"F0.wireOp",EDGE,"511e2649-3701-41cd-a2d4-a9df0a47a7a7.bottom")}),1.0]])]});
            var Q9;
            Q9=makeQuery(id+"F0.imprint","IMPRINT",FACE,{"disambiguationData":[TD([[makeQuery(id+"F0.imprint","IMPRINT",EDGE,{"derivedFrom":sQuery(id+"F0.wireOp",EDGE,"E68.bottom")}),1.0]])]});
            var Q10;
            Q10=makeQuery(id+"F0.imprint","IMPRINT",FACE,{"disambiguationData":[TD([[makeQuery(id+"F0.imprint","IMPRINT",EDGE,{"derivedFrom":sQuery(id+"F0.wireOp",EDGE,"E88.bottom")}),1.0]])]});
            extrude(context, id + "F1", {"entities" : qUnion([Q0, Q1, Q2, Q3, Q4, Q5, Q6, Q7, Q8, Q9, Q10]), "oppositeDirection" : true, "depth" : 4 * mm});
        }
    });
